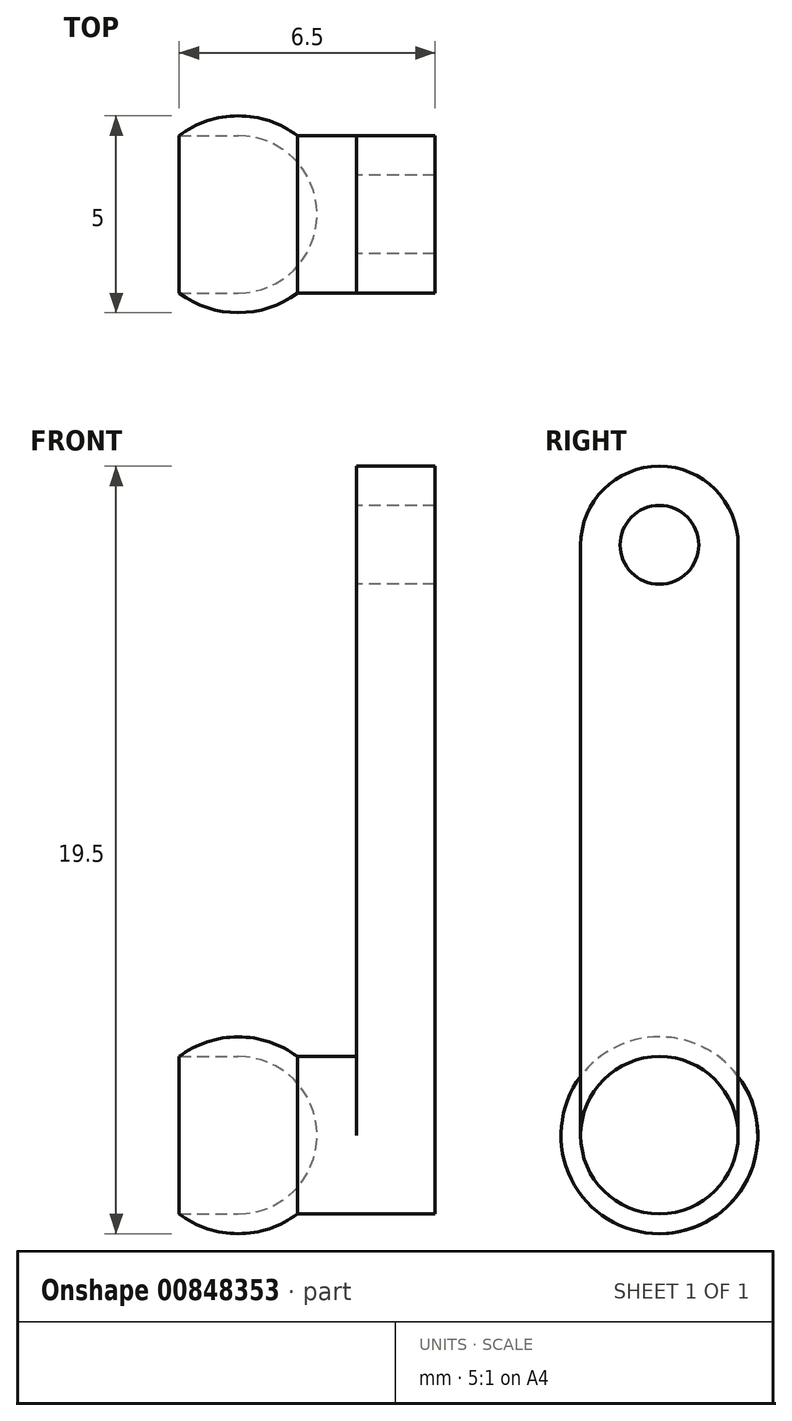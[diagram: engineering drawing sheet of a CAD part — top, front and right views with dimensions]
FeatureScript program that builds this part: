
annotation { "Feature Type Name" : "Feature", "Feature Type Description" : "" }
export const myFeature = defineFeature(function(context is Context, id is Id, definition is map)
    precondition{}
    {
        {
            var Q0;
            Q0=qCreatedBy(makeId("Right.planeOp"),FACE);
            var sketch = newSketch(context, id + "F0", { "sketchPlane" : qUnion([Q0])});
            skLineSegment(sketch, "E0", {"start": v(0, 2.5) * mm, "end": v(0, -2.5) * mm});
            skArc(sketch, "E1", {"start": v(0, -2.5) * mm, "mid": v(2.5, 0) * mm, "end": v(0, 2.5) * mm});
            skArc(sketch, "E2", {"start": v(0, -2) * mm, "mid": v(2, 0) * mm, "end": v(0, 2) * mm});
            skSolve(sketch);
        }
        {
            var Q0;
            {var subQ0=sQuery(id+"F0.wireOp",EDGE,"E1");Q0=makeQuery(id+"F0.imprint","IMPRINT",FACE,{"disambiguationData":[TD([[makeQuery(id+"F0.imprint","IMPRINT",EDGE,{"derivedFrom":subQ0}),1.0]])]});}
            var Q1;
            Q1=sQuery(id+"F0.wireOp",EDGE,"E0");
            revolve(context, id + "F1", {"surfaceOperationType" : NewSurfaceOperationType.NEW, "entities" : qUnion([Q0]), "axis" : qUnion([Q1]), "revolveType" : RevolveType.FULL});
        }
        {
            var Q0;
            Q0=qCreatedBy(makeId("Right.planeOp"),FACE);
            var sketch = newSketch(context, id + "F2", { "sketchPlane" : qUnion([Q0])});
            skCircle(sketch, "E3", {"center": v(0, 0) * mm, "radius": 2 * mm});
            skSolve(sketch);
        }
        {
            var Q0;
            Q0 = qSketchRegion(id + "F2", true);
            extrude(context, id + "F3", {"entities" : qUnion([Q0]), "operationType" : NewBodyOperationType.REMOVE, "oppositeDirection" : true, "depth" : 2.5 * mm, "offsetDistance" : 25 * mm});
        }
        {
            var Q0;
            Q0=qCreatedBy(makeId("Right.planeOp"),FACE);
            var sketch = newSketch(context, id + "F4", { "sketchPlane" : qUnion([Q0])});
            skCircle(sketch, "E4", {"center": v(0, 0) * mm, "radius": 2 * mm});
            skSolve(sketch);
        }
        {
            var Q0;
            Q0 = qSketchRegion(id + "F4", true);
            extrude(context, id + "F5", {"entities" : qUnion([Q0]), "operationType" : NewBodyOperationType.ADD, "depth" : 3 * mm, "offsetDistance" : 25 * mm});
        }
        {
            var Q0;
            Q0=makeQuery(id+"F5.opExtrude","CAP_FACE",FACE,{"disambiguationData":[OSD([sQuery(id+"F4.wireOp",EDGE,"E4")])],"isStart":false});
            var sketch = newSketch(context, id + "F6", { "sketchPlane" : qUnion([Q0])});
            skCircle(sketch, "E5", {"center": v(0, 0) * mm, "radius": 2 * mm});
            skCircle(sketch, "E6", {"center": v(0, 15) * mm, "radius": 2 * mm});
            skLineSegment(sketch, "E7", {"start": v(-2, 15) * mm, "end": v(-2, 0) * mm});
            skLineSegment(sketch, "E8", {"start": v(2, 0) * mm, "end": v(2, 15) * mm});
            skCircle(sketch, "E9", {"center": v(0, 15) * mm, "radius": 1 * mm});
            skSolve(sketch);
        }
        {
            var Q0;
            {var subQ0=sQuery(id+"F6.wireOp",EDGE,"E5");var subQ1=makeQuery(id+"F6.imprint","INTERSECT",VERTEX,{"derivedFrom":[subQ0,sQuery(id+"F6.wireOp",EDGE,"E7")]});Q0=makeQuery(id+"F6.imprint","IMPRINT",FACE,{"disambiguationData":[TD([[makeQuery(id+"F6.imprint","IMPRINT",EDGE,{"disambiguationData":[TD([[subQ1,1.0]])],"derivedFrom":subQ0}),1.0]])]});}
            var Q1;
            {var subQ0=sQuery(id+"F6.wireOp",EDGE,"E7");Q1=makeQuery(id+"F6.imprint","IMPRINT",FACE,{"disambiguationData":[TD([[makeQuery(id+"F6.imprint","IMPRINT",EDGE,{"derivedFrom":subQ0}),1.0]])]});}
            var Q2;
            Q2=makeQuery(id+"F6.imprint","IMPRINT",FACE,{"disambiguationData":[TD([[makeQuery(id+"F6.imprint","IMPRINT",EDGE,{"derivedFrom":sQuery(id+"F6.wireOp",EDGE,"E9")}),-1.0]])]});
            extrude(context, id + "F7", {"entities" : qUnion([Q0, Q1, Q2]), "operationType" : NewBodyOperationType.ADD, "depth" : 2 * mm, "offsetDistance" : 25 * mm});
        }
        {
            var Q0;
            Q0=makeQuery(id+"F5.opExtrude","CAP_FACE",FACE,{"disambiguationData":[OSD([sQuery(id+"F4.wireOp",EDGE,"E4")])],"isStart":true});
            var sketch = newSketch(context, id + "F8", { "sketchPlane" : qUnion([Q0])});
            skLineSegment(sketch, "E10", {"start": v(0, -2) * mm, "end": v(0, 2) * mm});
            skArc(sketch, "E11", {"start": v(0, -2) * mm, "mid": v(2, 0) * mm, "end": v(0, 2) * mm});
            skSolve(sketch);
        }
        {
            var Q0;
            Q0=makeQuery(id+"F8.imprint","IMPRINT",FACE,{"disambiguationData":[TD([[makeQuery(id+"F8.imprint","IMPRINT",EDGE,{"derivedFrom":sQuery(id+"F8.wireOp",EDGE,"E10")}),-1.0]])]});
            var Q1;
            Q1=sQuery(id+"F8.wireOp",EDGE,"E10");
            revolve(context, id + "F9", {"operationType" : NewBodyOperationType.REMOVE, "surfaceOperationType" : NewSurfaceOperationType.NEW, "entities" : qUnion([Q0]), "axis" : qUnion([Q1]), "revolveType" : RevolveType.FULL, "oppositeDirection" : true});
        }
    });
